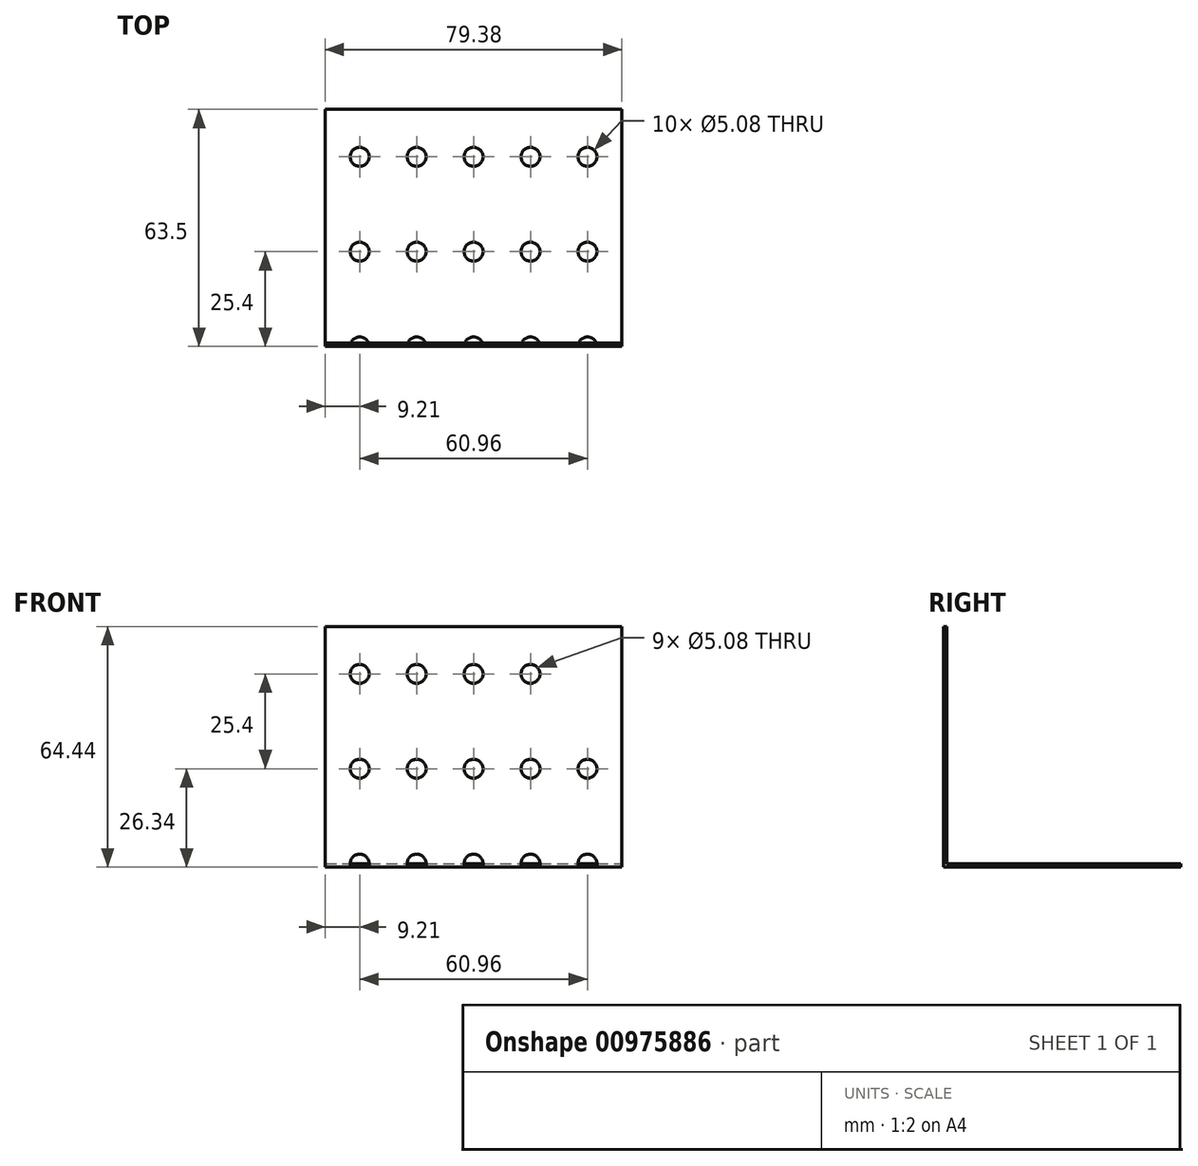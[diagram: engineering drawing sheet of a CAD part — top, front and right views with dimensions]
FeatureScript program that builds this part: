
annotation { "Feature Type Name" : "Feature", "Feature Type Description" : "" }
export const myFeature = defineFeature(function(context is Context, id is Id, definition is map)
    precondition{}
    {
        {
            var Q0;
            Q0=qCreatedBy(makeId("Front.planeOp"),FACE);
            var sketch = newSketch(context, id + "F0", { "sketchPlane" : qUnion([Q0])});
            skLineSegment(sketch, "E0.bottom", {"start": v(39.69, 63.5) * mm, "end": v(-39.69, 63.5) * mm});
            skLineSegment(sketch, "E0.left", {"start": v(39.69, 63.5) * mm, "end": v(39.69, 0) * mm});
            skLineSegment(sketch, "E0.right", {"start": v(-39.69, 63.5) * mm, "end": v(-39.69, 0) * mm});
            skPoint(sketch, "E0.middle", {"position": v(0, 0) * mm});
            skCircle(sketch, "E1", {"center": v(-30.48, 50.8) * mm, "radius": 2.54 * mm});
            skCircle(sketch, "E2.0.1.0", {"center": v(-30.48, 25.4) * mm, "radius": 2.54 * mm});
            skArc(sketch, "E2.0.2.0", {"start": v(-27.94, 0) * mm, "mid": v(-30.48, 2.54) * mm, "end": v(-33.02, 0) * mm});
            skCircle(sketch, "E2.1.0.0", {"center": v(-15.24, 50.8) * mm, "radius": 2.54 * mm});
            skCircle(sketch, "E2.1.1.0", {"center": v(-15.24, 25.4) * mm, "radius": 2.54 * mm});
            skArc(sketch, "E2.1.2.0", {"start": v(-12.7, 0) * mm, "mid": v(-15.24, 2.54) * mm, "end": v(-17.78, 0) * mm});
            skCircle(sketch, "E2.2.0.0", {"center": v(0, 50.8) * mm, "radius": 2.54 * mm});
            skCircle(sketch, "E2.2.1.0", {"center": v(0, 25.4) * mm, "radius": 2.54 * mm});
            skArc(sketch, "E2.2.2.0", {"start": v(2.54, 0) * mm, "mid": v(0, 2.54) * mm, "end": v(-2.54, 0) * mm});
            skLineSegment(sketch, "E2.direction1", {"start": v(-30.48, 50.8) * mm, "end": v(-15.24, 50.8) * mm, "construction": true});
            skLineSegment(sketch, "E2.direction2", {"start": v(-30.48, 50.8) * mm, "end": v(-30.48, 25.4) * mm, "construction": true});
            skCircle(sketch, "E3.0.3.0", {"center": v(15.24, 50.8) * mm, "radius": 2.54 * mm});
            skCircle(sketch, "E3.0.3.1", {"center": v(15.24, 25.4) * mm, "radius": 2.54 * mm});
            skArc(sketch, "E3.0.3.2", {"start": v(17.78, 0) * mm, "mid": v(15.24, 2.54) * mm, "end": v(12.7, 0) * mm});
            skCircle(sketch, "E3.0.4.1", {"center": v(30.48, 25.4) * mm, "radius": 2.54 * mm});
            skArc(sketch, "E3.0.4.2", {"start": v(33.02, 0) * mm, "mid": v(30.48, 2.54) * mm, "end": v(27.94, 0) * mm});
            skLineSegment(sketch, "E4", {"start": v(-39.69, 0) * mm, "end": v(-33.02, 0) * mm});
            skPoint(sketch, "E4.endSnap0", {"position": v(-39.69, 0) * mm});
            skPoint(sketch, "E0.top.end.orphan", {"position": v(-39.69, -63.5) * mm});
            skPoint(sketch, "E0.top.start.orphan", {"position": v(39.69, -63.5) * mm});
            skLineSegment(sketch, "E5.trimOffspring", {"start": v(-27.94, 0) * mm, "end": v(-17.78, 0) * mm});
            skLineSegment(sketch, "E6.trimOffspring", {"start": v(-12.7, 0) * mm, "end": v(-2.54, 0) * mm});
            skLineSegment(sketch, "E7.trimOffspring", {"start": v(2.54, 0) * mm, "end": v(12.7, 0) * mm});
            skLineSegment(sketch, "E8.trimOffspring", {"start": v(17.78, 0) * mm, "end": v(27.94, 0) * mm});
            skLineSegment(sketch, "E9.trimOffspring", {"start": v(33.02, 0) * mm, "end": v(39.69, 0) * mm});
            skSolve(sketch);
        }
        {
            var Q0;
            Q0=makeQuery(id+"F0.imprint","IMPRINT",FACE,{"disambiguationData":[TD([[makeQuery(id+"F0.imprint","IMPRINT",EDGE,{"derivedFrom":sQuery(id+"F0.wireOp",EDGE,"E0.bottom")}),1.0]])]});
            extrude(context, id + "F1", {"entities" : qUnion([Q0]), "oppositeDirection" : true, "depth" : 0.95 * mm, "offsetDistance" : 25.4 * mm});
        }
        {
            var Q0;
            Q0=qCreatedBy(makeId("Top.planeOp"),FACE);
            var sketch = newSketch(context, id + "F2", { "sketchPlane" : qUnion([Q0])});
            skLineSegment(sketch, "E10.bottom", {"start": v(39.69, 63.5) * mm, "end": v(-39.69, 63.5) * mm});
            skLineSegment(sketch, "E10.left", {"start": v(39.69, 63.5) * mm, "end": v(39.69, 0) * mm});
            skLineSegment(sketch, "E10.right", {"start": v(-39.69, 63.5) * mm, "end": v(-39.69, 0) * mm});
            skPoint(sketch, "E10.middle", {"position": v(0, 0) * mm});
            skCircle(sketch, "E11", {"center": v(-30.48, 50.8) * mm, "radius": 2.54 * mm});
            skCircle(sketch, "E12.0.1.0", {"center": v(-30.48, 25.4) * mm, "radius": 2.54 * mm});
            skArc(sketch, "E12.0.2.0", {"start": v(-27.94, 0) * mm, "mid": v(-30.48, 2.54) * mm, "end": v(-33.02, 0) * mm});
            skCircle(sketch, "E12.1.0.0", {"center": v(-15.24, 50.8) * mm, "radius": 2.54 * mm});
            skCircle(sketch, "E12.1.1.0", {"center": v(-15.24, 25.4) * mm, "radius": 2.54 * mm});
            skArc(sketch, "E12.1.2.0", {"start": v(-12.7, 0) * mm, "mid": v(-15.24, 2.54) * mm, "end": v(-17.78, 0) * mm});
            skCircle(sketch, "E12.2.0.0", {"center": v(0, 50.8) * mm, "radius": 2.54 * mm});
            skCircle(sketch, "E12.2.1.0", {"center": v(0, 25.4) * mm, "radius": 2.54 * mm});
            skArc(sketch, "E12.2.2.0", {"start": v(2.54, 0) * mm, "mid": v(0, 2.54) * mm, "end": v(-2.54, 0) * mm});
            skLineSegment(sketch, "E12.direction1", {"start": v(-30.48, 50.8) * mm, "end": v(-15.24, 50.8) * mm, "construction": true});
            skLineSegment(sketch, "E12.direction2", {"start": v(-30.48, 50.8) * mm, "end": v(-30.48, 25.4) * mm, "construction": true});
            skCircle(sketch, "E13.0.3.0", {"center": v(15.24, 50.8) * mm, "radius": 2.54 * mm});
            skCircle(sketch, "E13.0.3.1", {"center": v(15.24, 25.4) * mm, "radius": 2.54 * mm});
            skArc(sketch, "E13.0.3.2", {"start": v(17.78, 0) * mm, "mid": v(15.24, 2.54) * mm, "end": v(12.7, 0) * mm});
            skCircle(sketch, "E13.0.4.0", {"center": v(30.48, 50.8) * mm, "radius": 2.54 * mm});
            skCircle(sketch, "E13.0.4.1", {"center": v(30.48, 25.4) * mm, "radius": 2.54 * mm});
            skArc(sketch, "E13.0.4.2", {"start": v(33.02, 0) * mm, "mid": v(30.48, 2.54) * mm, "end": v(27.94, 0) * mm});
            skPoint(sketch, "E14.orphan", {"position": v(-39.69, -63.5) * mm});
            skPoint(sketch, "E15.orphan", {"position": v(39.69, -63.5) * mm});
            skLineSegment(sketch, "E16.trimOffspring", {"start": v(-27.94, 0) * mm, "end": v(-17.78, 0) * mm});
            skLineSegment(sketch, "E17.trimOffspring", {"start": v(-12.7, 0) * mm, "end": v(-2.54, 0) * mm});
            skLineSegment(sketch, "E18.trimOffspring", {"start": v(2.54, 0) * mm, "end": v(12.7, 0) * mm});
            skLineSegment(sketch, "E19.trimOffspring", {"start": v(17.78, 0) * mm, "end": v(27.94, 0) * mm});
            skLineSegment(sketch, "E20.trimOffspring", {"start": v(33.02, 0) * mm, "end": v(39.69, 0) * mm});
            skLineSegment(sketch, "E21", {"start": v(-39.69, 0) * mm, "end": v(-33.02, 0) * mm});
            skSolve(sketch);
        }
        {
            var Q0;
            Q0 = qSketchRegion(id + "F2", true);
            extrude(context, id + "F3", {"entities" : qUnion([Q0]), "operationType" : NewBodyOperationType.ADD, "oppositeDirection" : true, "depth" : 0.94 * mm, "offsetDistance" : 25.4 * mm});
        }
    });
